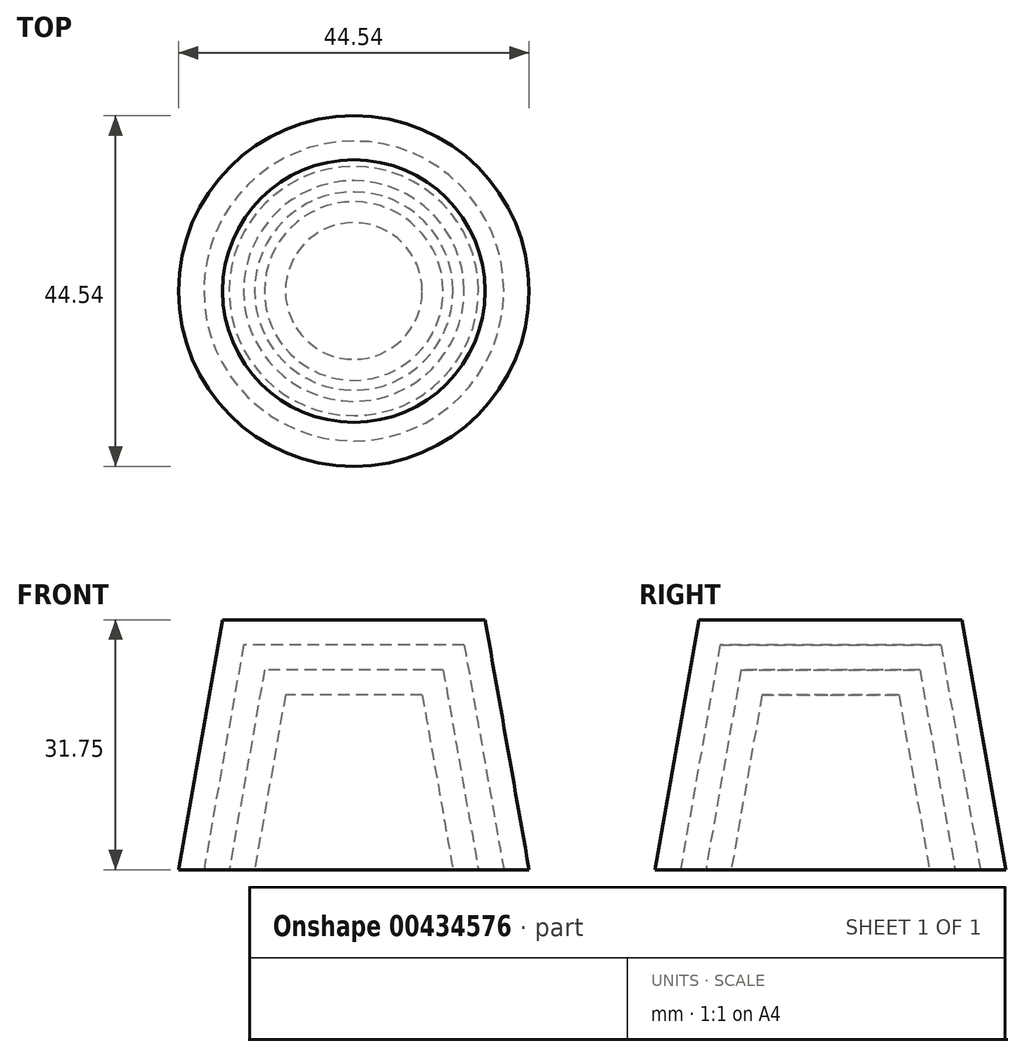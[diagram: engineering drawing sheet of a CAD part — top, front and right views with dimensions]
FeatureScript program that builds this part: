
annotation { "Feature Type Name" : "Feature", "Feature Type Description" : "" }
export const myFeature = defineFeature(function(context is Context, id is Id, definition is map)
    precondition{}
    {
        {
            var Q0;
            Q0=qCreatedBy(makeId("Front.planeOp"),FACE);
            var sketch = newSketch(context, id + "F0", { "sketchPlane" : qUnion([Q0])});
            skLineSegment(sketch, "E0", {"start": v(19.05, 0) * mm, "end": v(14.01, 28.58) * mm});
            skLineSegment(sketch, "E1", {"start": v(14.01, 28.58) * mm, "end": v(0, 28.58) * mm});
            skLineSegment(sketch, "E2.0", {"start": v(16.68, 31.75) * mm, "end": v(0, 31.75) * mm});
            skLineSegment(sketch, "E2.1", {"start": v(22.27, 0) * mm, "end": v(16.68, 31.75) * mm});
            skLineSegment(sketch, "E3", {"start": v(0, 31.75) * mm, "end": v(0, 28.58) * mm});
            skLineSegment(sketch, "E4", {"start": v(19.05, 0) * mm, "end": v(22.27, 0) * mm});
            skLineSegment(sketch, "E5.0", {"start": v(11.35, 25.4) * mm, "end": v(0, 25.4) * mm});
            skLineSegment(sketch, "E5.1", {"start": v(15.83, 0) * mm, "end": v(11.35, 25.4) * mm});
            skLineSegment(sketch, "E6.0", {"start": v(8.68, 22.23) * mm, "end": v(0, 22.23) * mm});
            skLineSegment(sketch, "E6.1", {"start": v(12.6, 0) * mm, "end": v(8.68, 22.23) * mm});
            skLineSegment(sketch, "E7", {"start": v(12.6, 0) * mm, "end": v(15.83, 0) * mm});
            skLineSegment(sketch, "E8", {"start": v(0, 25.4) * mm, "end": v(0, 22.23) * mm});
            skSolve(sketch);
        }
        {
            var Q0;
            Q0 = qSketchRegion(id + "F0", true);
            var Q1;
            Q1=sQuery(id+"F0.wireOp",EDGE,"E3");
            revolve(context, id + "F1", {"entities" : qUnion([Q0]), "axis" : qUnion([Q1]), "revolveType" : RevolveType.FULL});
        }
    });
